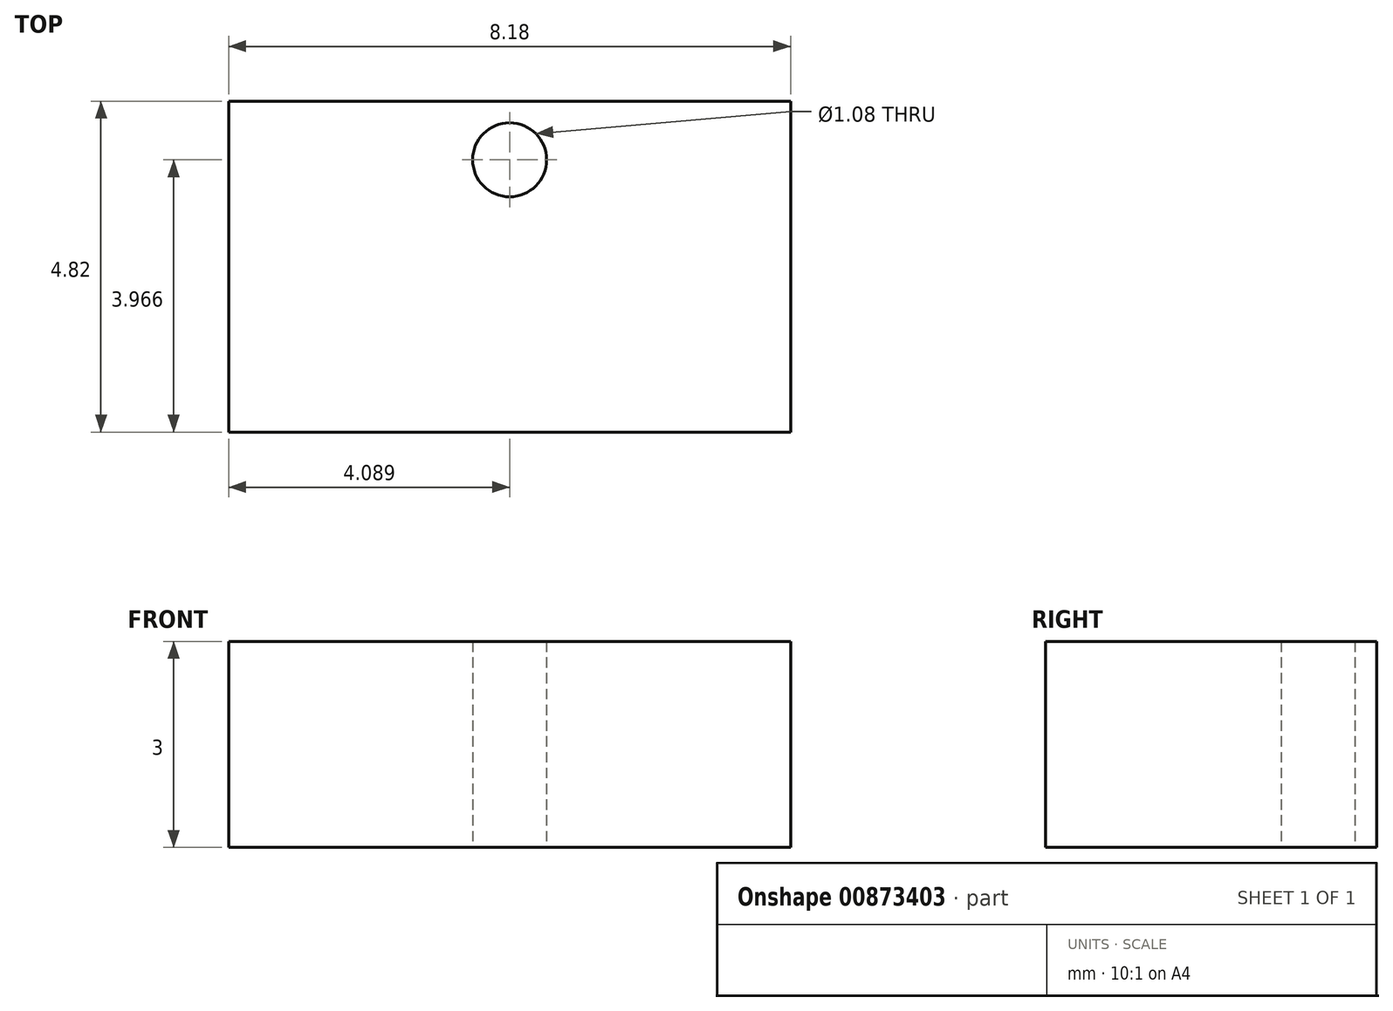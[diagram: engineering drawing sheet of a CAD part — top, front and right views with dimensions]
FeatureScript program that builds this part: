
annotation { "Feature Type Name" : "Feature", "Feature Type Description" : "" }
export const myFeature = defineFeature(function(context is Context, id is Id, definition is map)
    precondition{}
    {
        {
            var Q0;
            Q0=qCreatedBy(makeId("Top.planeOp"),FACE);
            var sketch = newSketch(context, id + "F0", { "sketchPlane" : qUnion([Q0])});
            skLineSegment(sketch, "E0", {"start": v(0, 0) * mm, "end": v(8.18, 0) * mm});
            skLineSegment(sketch, "E1", {"start": v(8.18, 0) * mm, "end": v(8.18, 4.82) * mm});
            skLineSegment(sketch, "E2", {"start": v(8.18, 4.82) * mm, "end": v(0, 4.82) * mm});
            skLineSegment(sketch, "E3", {"start": v(0, 4.82) * mm, "end": v(0, 0) * mm});
            skCircle(sketch, "E4", {"center": v(4.09, 3.97) * mm, "radius": 0.54 * mm});
            skPoint(sketch, "E4.centerSnap0", {"position": v(4.09, 4.82) * mm});
            skSolve(sketch);
        }
        {
            var Q0;
            Q0 = qSketchRegion(id + "F0", true);
            extrude(context, id + "F1", {"entities" : qUnion([Q0]), "depth" : 3 * mm, "offsetDistance" : 25 * mm});
        }
    });
